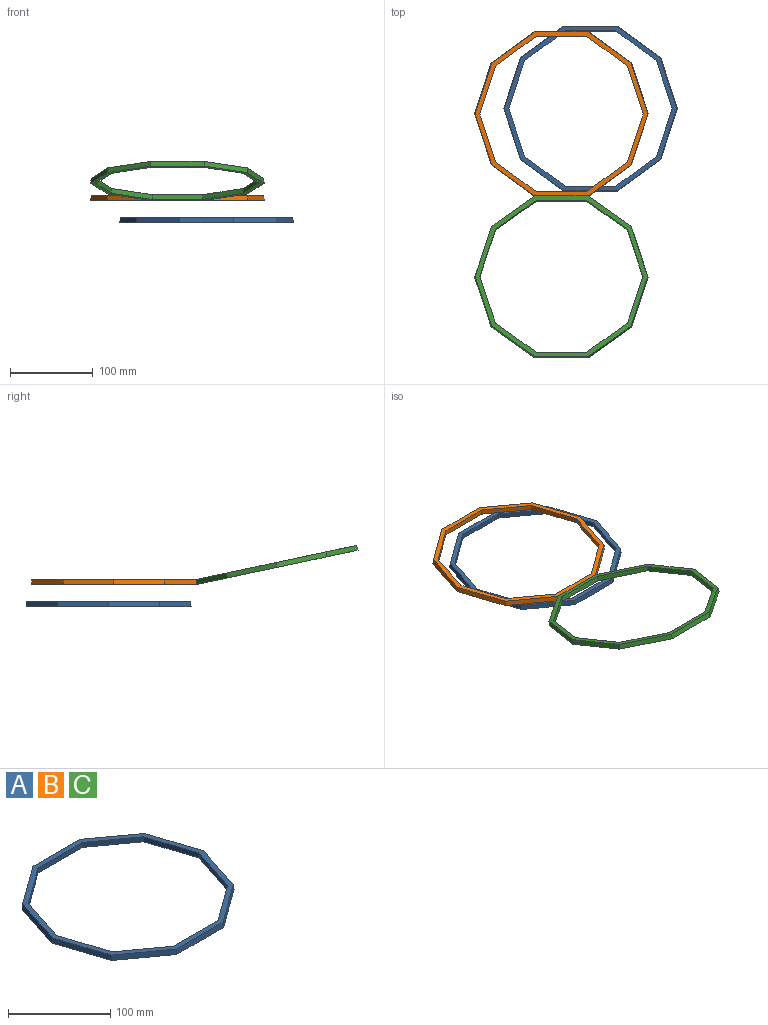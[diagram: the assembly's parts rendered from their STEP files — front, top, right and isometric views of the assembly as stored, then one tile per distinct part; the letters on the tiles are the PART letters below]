
ASSEMBLY  parts=3 mates=1
PART A: 22 faces, bbox 210.3x200x6 mm
  f0: plane 58.1x18.88mm, normal (-0.95,-0.31,0), area 366.5mm2, adj f1,f9,f10,f11
  f1: plane 58.1x18.88mm, normal (-0.95,0.31,0), area 366.5mm2, adj f0,f2,f10,f11
  f2: plane 49.42x35.91mm, normal (-0.59,0.81,0), area 366.5mm2, adj f1,f3,f10,f11
  f3: plane 61.09x6mm, normal (0,1,0), area 366.5mm2, adj f2,f4,f10,f11
  f4: plane 49.42x35.91mm, normal (0.59,0.81,0), area 366.5mm2, adj f3,f5,f10,f11
  f5: plane 58.1x18.88mm, normal (0.95,0.31,0), area 366.5mm2, adj f4,f6,f10,f11
  f6: plane 58.1x18.88mm, normal (0.95,-0.31,0), area 366.5mm2, adj f5,f7,f10,f11
  f7: plane 49.42x35.91mm, normal (0.59,-0.81,0), area 366.5mm2, adj f6,f8,f10,f11
  f8: plane 61.09x6mm, normal (0,-1,0), area 366.5mm2, adj f7,f9,f10,f11
  f9: plane 49.42x35.91mm, normal (-0.59,-0.81,0), area 366.5mm2, adj f0,f8,f10,f11
  f10: plane 208.97x198.74mm, normal (0,0,1), area 3373.6mm2, adj f0,f1,f2,f3,f4,f5,f6,f7
  f11: plane 210.29x200mm, normal (0,0,-1), area 3782.1mm2, adj f0,f1,f2,f3,f4,f5,f6,f7
  f12: plane 52.78x38.59mm, normal (0.58,0.8,0.1), area 390.8mm2, adj f10,f11,f13,f14
  f13: plane 61.8x20.62mm, normal (0.95,0.31,0.1), area 390.8mm2, adj f10,f11,f12,f15
  f14: plane 64.98x6mm, normal (0,0.99,0.1), area 390.8mm2, adj f10,f11,f12,f16
  f15: plane 61.8x20.62mm, normal (0.95,-0.31,0.1), area 390.8mm2, adj f10,f11,f13,f17
  f16: plane 52.78x38.59mm, normal (-0.58,0.8,0.1), area 390.8mm2, adj f10,f11,f14,f18
  f17: plane 52.78x38.59mm, normal (0.58,-0.8,0.1), area 390.8mm2, adj f10,f11,f15,f19
  f18: plane 61.8x20.62mm, normal (-0.95,0.31,0.1), area 390.8mm2, adj f10,f11,f16,f20
  f19: plane 64.98x6mm, normal (0,-0.99,0.1), area 390.8mm2, adj f10,f11,f17,f21
  f20: plane 61.8x20.62mm, normal (-0.95,-0.31,0.1), area 390.8mm2, adj f10,f11,f18,f21
  f21: plane 52.78x38.59mm, normal (-0.58,-0.8,0.1), area 390.8mm2, adj f10,f11,f19,f20
PART B: same geometry as A
PART C: same geometry as A
PLACE A t=(40.45,4.51,-31.26)mm
PLACE B t=(5.13,-2.05,-4.53)mm fixed
PLACE C rot(axis=(0,0.1,0.99),180deg) t=(5.13,-199.87,16.27)mm
MATE fastened B.f19 <-> C.f19  axis (0,-0.99,0.1) through (5.13,-101.74,-1.53)mm
